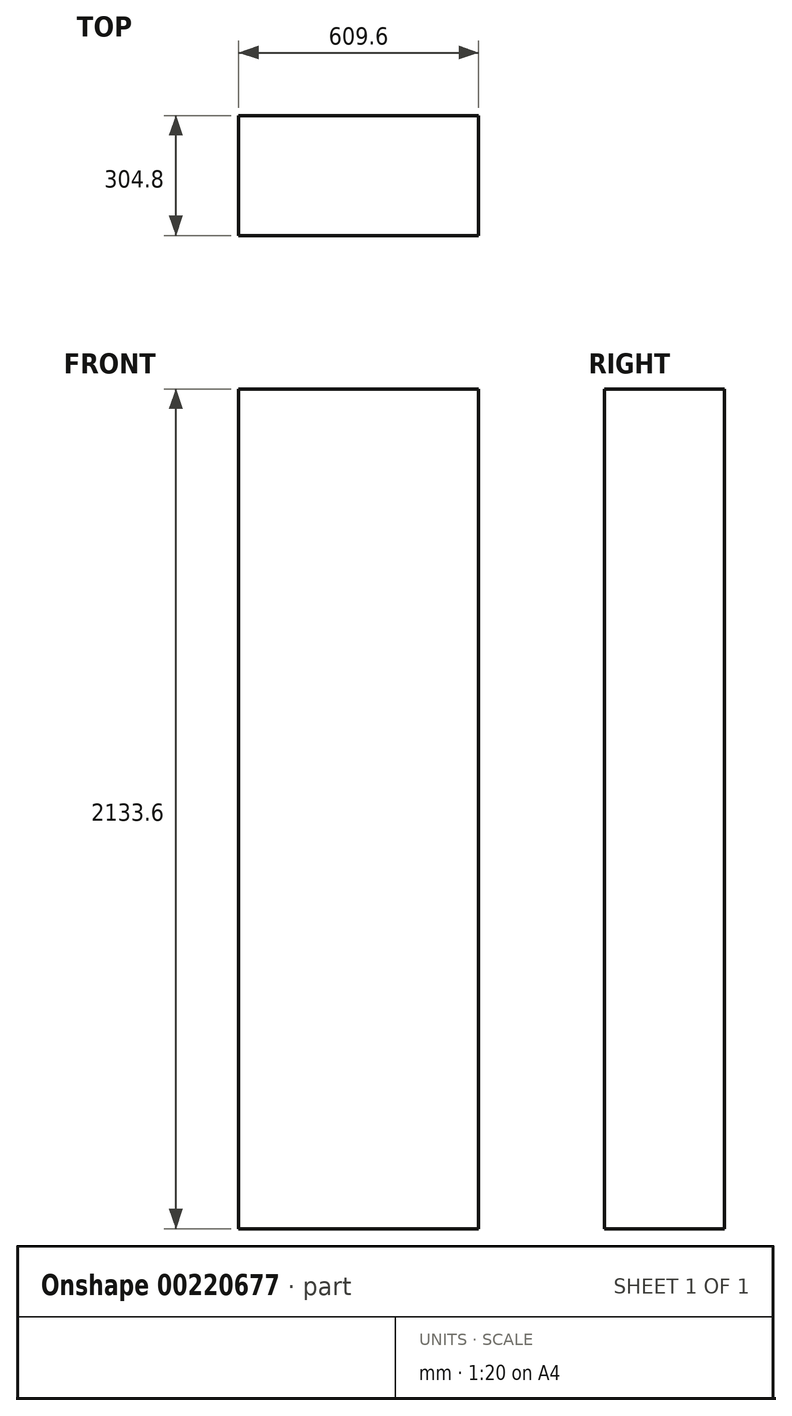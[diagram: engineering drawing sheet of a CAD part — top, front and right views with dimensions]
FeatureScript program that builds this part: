
annotation { "Feature Type Name" : "Feature", "Feature Type Description" : "" }
export const myFeature = defineFeature(function(context is Context, id is Id, definition is map)
    precondition{}
    {
        {
            var Q0;
            Q0=qCreatedBy(makeId("Top.planeOp"),FACE);
            var sketch = newSketch(context, id + "F0", { "sketchPlane" : qUnion([Q0])});
            skLineSegment(sketch, "E0.bottom", {"start": v(152.4, -364.72) * mm, "end": v(-152.4, -364.72) * mm});
            skLineSegment(sketch, "E0.top", {"start": v(152.4, 364.72) * mm, "end": v(-152.4, 364.72) * mm});
            skLineSegment(sketch, "E0.left", {"start": v(152.4, -364.72) * mm, "end": v(152.4, 364.72) * mm});
            skLineSegment(sketch, "E0.right", {"start": v(-152.4, -364.72) * mm, "end": v(-152.4, 364.72) * mm});
            skPoint(sketch, "E0.middle", {"position": v(0, 0) * mm});
            skSolve(sketch);
        }
        {
            var Q0;
            Q0 = qSketchRegion(id + "F0", true);
            extrude(context, id + "F1", {"entities" : qUnion([Q0]), "depth" : 2133.6 * mm});
        }
        {
            var Q0;
            Q0=makeQuery(id+"F1.opExtrude","SWEPT_BODY",BODY,{"disambiguationData":[OSD([sQuery(id+"F0.wireOp",EDGE,"E0.bottom"),sQuery(id+"F0.wireOp",EDGE,"E0.top"),sQuery(id+"F0.wireOp",EDGE,"E0.left"),sQuery(id+"F0.wireOp",EDGE,"E0.right")])]});
            deleteBodies(context, id + "F2", {"entities" : qUnion([Q0])});
        }
        {
            var Q0;
            Q0=qCreatedBy(makeId("Top.planeOp"),FACE);
            var sketch = newSketch(context, id + "F3", { "sketchPlane" : qUnion([Q0])});
            skLineSegment(sketch, "E1.bottom", {"start": v(304.8, -152.4) * mm, "end": v(-304.8, -152.4) * mm});
            skLineSegment(sketch, "E1.top", {"start": v(304.8, 152.4) * mm, "end": v(-304.8, 152.4) * mm});
            skLineSegment(sketch, "E1.left", {"start": v(304.8, -152.4) * mm, "end": v(304.8, 152.4) * mm});
            skLineSegment(sketch, "E1.right", {"start": v(-304.8, -152.4) * mm, "end": v(-304.8, 152.4) * mm});
            skPoint(sketch, "E1.middle", {"position": v(0, 0) * mm});
            skSolve(sketch);
        }
        {
            var Q0;
            Q0=makeQuery(id+"F3.imprint","IMPRINT",FACE,{"disambiguationData":[TD([[makeQuery(id+"F3.imprint","IMPRINT",EDGE,{"derivedFrom":sQuery(id+"F3.wireOp",EDGE,"E1.bottom")}),-1.0]])]});
            extrude(context, id + "F4", {"entities" : qUnion([Q0]), "depth" : 2133.6 * mm});
        }
    });
